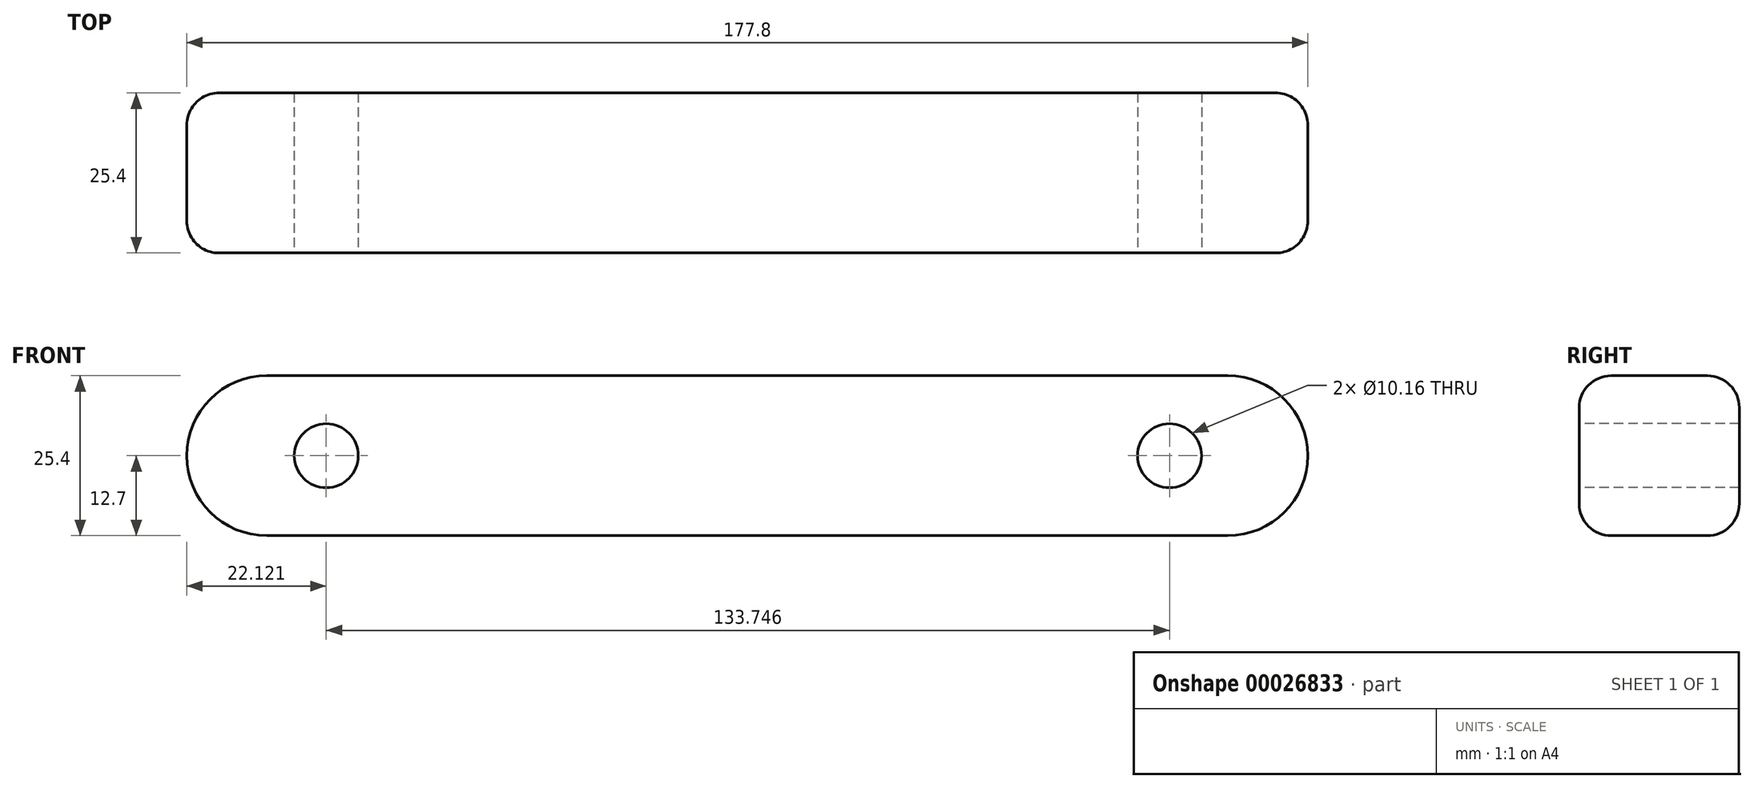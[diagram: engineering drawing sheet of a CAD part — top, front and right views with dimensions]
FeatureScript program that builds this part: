
annotation { "Feature Type Name" : "Feature", "Feature Type Description" : "" }
export const myFeature = defineFeature(function(context is Context, id is Id, definition is map)
    precondition{}
    {
        {
            var Q0;
            Q0=qCreatedBy(makeId("Top.planeOp"),FACE);
            var sketch = newSketch(context, id + "F0", { "sketchPlane" : qUnion([Q0])});
            skLineSegment(sketch, "E0.rect.bottom", {"start": v(-88.9, 12.7) * mm, "end": v(88.9, 12.7) * mm});
            skLineSegment(sketch, "E0.rect.top", {"start": v(-88.9, -12.7) * mm, "end": v(88.9, -12.7) * mm});
            skLineSegment(sketch, "E0.rect.left", {"start": v(-88.9, 12.7) * mm, "end": v(-88.9, -12.7) * mm});
            skLineSegment(sketch, "E0.rect.right", {"start": v(88.9, 12.7) * mm, "end": v(88.9, -12.7) * mm});
            skPoint(sketch, "E0.rect.middle", {"position": v(0, 0) * mm});
            skSolve(sketch);
        }
        {
            var Q0;
            Q0=makeQuery(id+"F0.imprint","IMPRINT",FACE,{"disambiguationData":[TD([[makeQuery(id+"F0.imprint","IMPRINT",EDGE,{"derivedFrom":sQuery(id+"F0.wireOp",EDGE,"E0.rect.bottom")}),-1.0]])]});
            extrude(context, id + "F1", {"entities" : qUnion([Q0]), "depth" : 25.4 * mm});
        }
        {
            var Q0;
            Q0=makeQuery(id+"F1.opExtrude","CAP_EDGE",EDGE,{"disambiguationData":[OSD([sQuery(id+"F0.wireOp",EDGE,"E0.rect.right")])],"isStart":false});
            var Q1;
            Q1=makeQuery(id+"F1.opExtrude","CAP_EDGE",EDGE,{"disambiguationData":[OSD([sQuery(id+"F0.wireOp",EDGE,"E0.rect.right")])],"isStart":true});
            var Q2;
            Q2=makeQuery(id+"F1.opExtrude","CAP_EDGE",EDGE,{"disambiguationData":[OSD([sQuery(id+"F0.wireOp",EDGE,"E0.rect.left")])],"isStart":true});
            var Q3;
            Q3=makeQuery(id+"F1.opExtrude","CAP_EDGE",EDGE,{"disambiguationData":[OSD([sQuery(id+"F0.wireOp",EDGE,"E0.rect.left")])],"isStart":false});
            fillet(context, id + "F2", {"entities" : qUnion([Q0, Q1, Q2, Q3]), "radius" : 12.7 * mm, "tangentPropagation" : true, "allowEdgeOverflow" : false});
        }
        {
            var Q0;
            Q0=makeQuery(id+"F1.opExtrude","SWEPT_FACE",FACE,{"disambiguationData":[OSD([sQuery(id+"F0.wireOp",EDGE,"E0.rect.top")])]});
            var sketch = newSketch(context, id + "F3", { "sketchPlane" : qUnion([Q0])});
            skCircle(sketch, "E1", {"center": v(66.97, 12.7) * mm, "radius": 5.08 * mm});
            skCircle(sketch, "E2", {"center": v(-66.78, 12.7) * mm, "radius": 5.08 * mm});
            skSolve(sketch);
        }
        {
            var Q0;
            Q0=makeQuery(id+"F3.imprint","IMPRINT",FACE,{"disambiguationData":[TD([[makeQuery(id+"F3.imprint","IMPRINT",EDGE,{"derivedFrom":sQuery(id+"F3.wireOp",EDGE,"E2")}),1.0]])]});
            var Q1;
            Q1=makeQuery(id+"F3.imprint","IMPRINT",FACE,{"disambiguationData":[TD([[makeQuery(id+"F3.imprint","IMPRINT",EDGE,{"derivedFrom":sQuery(id+"F3.wireOp",EDGE,"E1")}),1.0]])]});
            extrude(context, id + "F4", {"entities" : qUnion([Q0, Q1]), "operationType" : NewBodyOperationType.REMOVE, "oppositeDirection" : true, "depth" : 25.4 * mm});
        }
        {
            var Q0;
            Q0=makeQuery(id+"F1.opExtrude","CAP_EDGE",EDGE,{"disambiguationData":[OSD([sQuery(id+"F0.wireOp",EDGE,"E0.rect.top")])],"isStart":false});
            var Q1;
            Q1=makeQuery(id+"F1.opExtrude","CAP_EDGE",EDGE,{"disambiguationData":[OSD([sQuery(id+"F0.wireOp",EDGE,"E0.rect.bottom")])],"isStart":false});
            var Q2;
            Q2=makeQuery(id+"F1.opExtrude","CAP_EDGE",EDGE,{"disambiguationData":[OSD([sQuery(id+"F0.wireOp",EDGE,"E0.rect.top")])],"isStart":true});
            var Q3;
            Q3=makeQuery(id+"F1.opExtrude","CAP_EDGE",EDGE,{"disambiguationData":[OSD([sQuery(id+"F0.wireOp",EDGE,"E0.rect.bottom")])],"isStart":true});
            fillet(context, id + "F5", {"entities" : qUnion([Q0, Q1, Q2, Q3]), "radius" : 5.08 * mm, "tangentPropagation" : true, "allowEdgeOverflow" : false});
        }
    });
